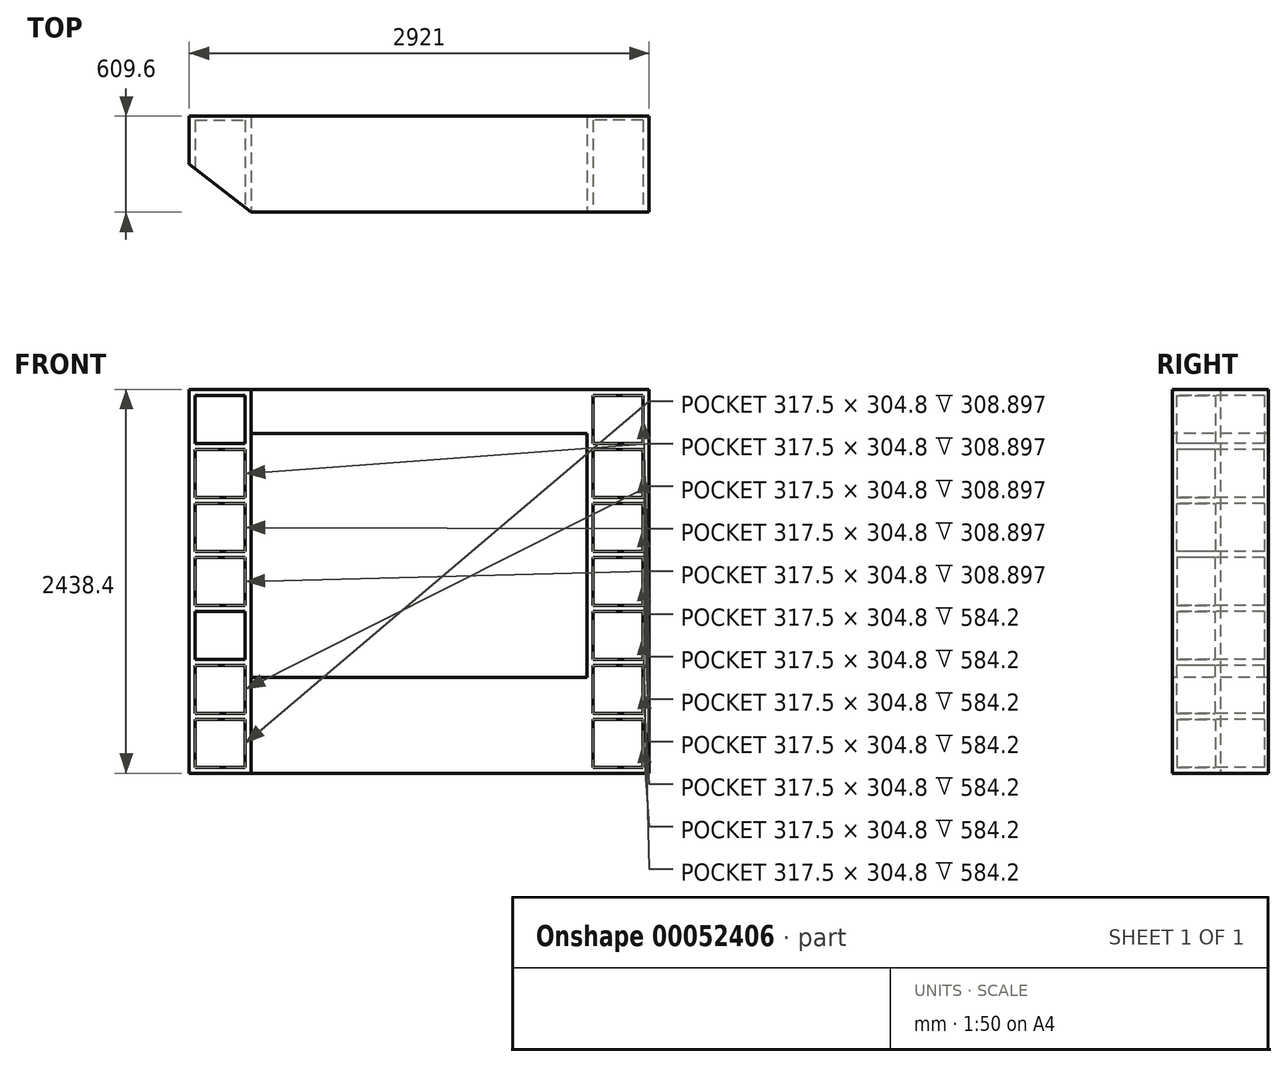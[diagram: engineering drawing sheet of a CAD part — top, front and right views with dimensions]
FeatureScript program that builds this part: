
annotation { "Feature Type Name" : "Feature", "Feature Type Description" : "" }
export const myFeature = defineFeature(function(context is Context, id is Id, definition is map)
    precondition{}
    {
        {
            var Q0;
            Q0=qCreatedBy(makeId("Top.planeOp"),FACE);
            var sketch = newSketch(context, id + "F0", { "sketchPlane" : qUnion([Q0])});
            skLineSegment(sketch, "E0", {"start": v(-1460.5, 0) * mm, "end": v(1460.5, 0) * mm});
            skLineSegment(sketch, "E1", {"start": v(-1460.5, 0) * mm, "end": v(-1460.5, -304.8) * mm});
            skLineSegment(sketch, "E2", {"start": v(1460.5, 0) * mm, "end": v(1460.5, -304.8) * mm});
            skLineSegment(sketch, "E3", {"start": v(-1066.8, -609.6) * mm, "end": v(-1460.5, -304.8) * mm});
            skLineSegment(sketch, "E4", {"start": v(0, -609.6) * mm, "end": v(1460.5, -609.6) * mm});
            skLineSegment(sketch, "E5", {"start": v(0, -609.6) * mm, "end": v(-1066.8, -609.6) * mm});
            skLineSegment(sketch, "E6", {"start": v(1460.5, -304.8) * mm, "end": v(1460.5, -609.6) * mm});
            skPoint(sketch, "E7.start.orphan", {"position": v(1066.8, -609.6) * mm});
            skSolve(sketch);
        }
        {
            var Q0;
            Q0=makeQuery(id+"F0.imprint","IMPRINT",FACE,{"disambiguationData":[TD([[makeQuery(id+"F0.imprint","IMPRINT",EDGE,{"derivedFrom":sQuery(id+"F0.wireOp",EDGE,"E0")}),-1.0]])]});
            extrude(context, id + "F1", {"entities" : qUnion([Q0]), "depth" : 2438.4 * mm});
        }
        {
            var Q0;
            Q0=makeQuery(id+"F1.opExtrude","SWEPT_FACE",FACE,{"disambiguationData":[OSD([sQuery(id+"F0.wireOp",EDGE,"E4"),sQuery(id+"F0.wireOp",EDGE,"E5")])]});
            var sketch = newSketch(context, id + "F2", { "sketchPlane" : qUnion([Q0])});
            skLineSegment(sketch, "E8", {"start": v(-1066.8, 609.6) * mm, "end": v(-1066.8, 2159) * mm});
            skLineSegment(sketch, "E9", {"start": v(-1066.8, 2159) * mm, "end": v(1066.8, 2159) * mm});
            skLineSegment(sketch, "E10", {"start": v(1066.8, 609.6) * mm, "end": v(-1066.8, 609.6) * mm});
            skLineSegment(sketch, "E11", {"start": v(1066.8, 2159) * mm, "end": v(1066.8, 609.6) * mm});
            skSolve(sketch);
        }
        {
            var Q0;
            Q0=makeQuery(id+"F2.imprint","IMPRINT",FACE,{"disambiguationData":[TD([[makeQuery(id+"F2.imprint","IMPRINT",EDGE,{"derivedFrom":sQuery(id+"F2.wireOp",EDGE,"E8")}),1.0]])]});
            extrude(context, id + "F3", {"entities" : qUnion([Q0]), "operationType" : NewBodyOperationType.REMOVE, "oppositeDirection" : true, "depth" : 609.6 * mm});
        }
        {
            var Q0;
            {var subQ2=sQuery(id+"F0.wireOp",EDGE,"E5");var subQ3=sQuery(id+"F0.wireOp",EDGE,"E4");Q0=makeQuery(id+"F3.boolean.opBoolean","SPLIT",FACE,{"disambiguationData":[TD([makeQuery(id+"F3.opExtrude","SWEPT_FACE",FACE,{"disambiguationData":[OSD([sQuery(id+"F2.wireOp",EDGE,"E10")])]})])],"derivedFrom":makeQuery(id+"F1.opExtrude","SWEPT_FACE",FACE,{"disambiguationData":[OSD([subQ3,subQ2])]})});}
            var sketch = newSketch(context, id + "F4", { "sketchPlane" : qUnion([Q0])});
            skLineSegment(sketch, "E12", {"start": v(1104.9, 38.1) * mm, "end": v(1422.4, 38.1) * mm});
            skLineSegment(sketch, "E13", {"start": v(1104.9, 342.9) * mm, "end": v(1422.4, 342.9) * mm});
            skLineSegment(sketch, "E14", {"start": v(1422.4, 342.9) * mm, "end": v(1104.9, 342.9) * mm});
            skLineSegment(sketch, "E15", {"start": v(1104.9, 1028.7) * mm, "end": v(1422.4, 1028.7) * mm});
            skLineSegment(sketch, "E16", {"start": v(1104.9, 342.9) * mm, "end": v(1104.9, 38.1) * mm});
            skLineSegment(sketch, "E17", {"start": v(1422.4, 342.9) * mm, "end": v(1422.4, 38.1) * mm});
            skLineSegment(sketch, "E18", {"start": v(1104.9, 381) * mm, "end": v(1422.4, 381) * mm});
            skLineSegment(sketch, "E19", {"start": v(1422.4, 381) * mm, "end": v(1422.4, 685.8) * mm});
            skLineSegment(sketch, "E20", {"start": v(1104.9, 381) * mm, "end": v(1104.9, 685.8) * mm});
            skLineSegment(sketch, "E21", {"start": v(1422.4, 685.8) * mm, "end": v(1104.9, 685.8) * mm});
            skLineSegment(sketch, "E22", {"start": v(1104.9, 723.9) * mm, "end": v(1422.4, 723.9) * mm});
            skLineSegment(sketch, "E23", {"start": v(1422.4, 723.9) * mm, "end": v(1422.4, 1028.7) * mm});
            skLineSegment(sketch, "E24", {"start": v(1104.9, 1028.7) * mm, "end": v(1104.9, 723.9) * mm});
            skLineSegment(sketch, "E25", {"start": v(1104.9, 1066.8) * mm, "end": v(1422.4, 1066.8) * mm});
            skLineSegment(sketch, "E26", {"start": v(1422.4, 1066.8) * mm, "end": v(1422.4, 1371.6) * mm});
            skLineSegment(sketch, "E27", {"start": v(1422.4, 1371.6) * mm, "end": v(1104.9, 1371.6) * mm});
            skLineSegment(sketch, "E28", {"start": v(1104.9, 1371.6) * mm, "end": v(1104.9, 1066.8) * mm});
            skLineSegment(sketch, "E29", {"start": v(1422.4, 1409.7) * mm, "end": v(1104.9, 1409.7) * mm});
            skLineSegment(sketch, "E30", {"start": v(1104.9, 1409.7) * mm, "end": v(1104.9, 1714.5) * mm});
            skLineSegment(sketch, "E31", {"start": v(1104.9, 1714.5) * mm, "end": v(1422.4, 1714.5) * mm});
            skLineSegment(sketch, "E32", {"start": v(1422.4, 1714.5) * mm, "end": v(1422.4, 1409.7) * mm});
            skLineSegment(sketch, "E33", {"start": v(1104.9, 1752.6) * mm, "end": v(1422.4, 1752.6) * mm});
            skLineSegment(sketch, "E34", {"start": v(1422.4, 1752.6) * mm, "end": v(1422.4, 2057.4) * mm});
            skLineSegment(sketch, "E35", {"start": v(1422.4, 2057.4) * mm, "end": v(1104.9, 2057.4) * mm});
            skLineSegment(sketch, "E36", {"start": v(1104.9, 2057.4) * mm, "end": v(1104.9, 1752.6) * mm});
            skLineSegment(sketch, "E37", {"start": v(1422.4, 2095.5) * mm, "end": v(1104.9, 2095.5) * mm});
            skLineSegment(sketch, "E38", {"start": v(1104.9, 2095.5) * mm, "end": v(1104.9, 2400.3) * mm});
            skLineSegment(sketch, "E39", {"start": v(1104.9, 2400.3) * mm, "end": v(1422.4, 2400.3) * mm});
            skLineSegment(sketch, "E40", {"start": v(1422.4, 2400.3) * mm, "end": v(1422.4, 2095.5) * mm});
            skLineSegment(sketch, "E41", {"start": v(1066.8, 609.6) * mm, "end": v(1066.8, 1171.43) * mm});
            skLineSegment(sketch, "E42", {"start": v(0, 0) * mm, "end": v(0, 823.78) * mm});
            skLineSegment(sketch, "E43.MirrorCS", {"start": v(-1422.4, 2095.5) * mm, "end": v(-1104.9, 2095.5) * mm});
            skLineSegment(sketch, "E44.MirrorCS", {"start": v(-1422.4, 685.8) * mm, "end": v(-1104.9, 685.8) * mm});
            skLineSegment(sketch, "E45.MirrorCS", {"start": v(-1422.4, 2057.4) * mm, "end": v(-1104.9, 2057.4) * mm});
            skLineSegment(sketch, "E46.MirrorCS", {"start": v(-1104.9, 342.9) * mm, "end": v(-1422.4, 342.9) * mm});
            skLineSegment(sketch, "E47.MirrorCS", {"start": v(-1104.9, 723.9) * mm, "end": v(-1422.4, 723.9) * mm});
            skLineSegment(sketch, "E48.MirrorCS", {"start": v(-1104.9, 2095.5) * mm, "end": v(-1104.9, 2400.3) * mm});
            skLineSegment(sketch, "E49.MirrorCS", {"start": v(-1422.4, 723.9) * mm, "end": v(-1422.4, 1028.7) * mm});
            skLineSegment(sketch, "E50.MirrorCS", {"start": v(-1422.4, 342.9) * mm, "end": v(-1422.4, 38.1) * mm});
            skLineSegment(sketch, "E51.MirrorCS", {"start": v(-1104.9, 1028.7) * mm, "end": v(-1104.9, 723.9) * mm});
            skLineSegment(sketch, "E52.MirrorCS", {"start": v(-1104.9, 1752.6) * mm, "end": v(-1422.4, 1752.6) * mm});
            skLineSegment(sketch, "E53.MirrorCS", {"start": v(-1422.4, 1409.7) * mm, "end": v(-1104.9, 1409.7) * mm});
            skLineSegment(sketch, "E54.MirrorCS", {"start": v(-1104.9, 1409.7) * mm, "end": v(-1104.9, 1714.5) * mm});
            skLineSegment(sketch, "E55.MirrorCS", {"start": v(-1422.4, 1752.6) * mm, "end": v(-1422.4, 2057.4) * mm});
            skLineSegment(sketch, "E56.MirrorCS", {"start": v(-1104.9, 381) * mm, "end": v(-1104.9, 685.8) * mm});
            skLineSegment(sketch, "E57.MirrorCS", {"start": v(-1422.4, 381) * mm, "end": v(-1422.4, 685.8) * mm});
            skLineSegment(sketch, "E58.MirrorCS", {"start": v(-1104.9, 381) * mm, "end": v(-1422.4, 381) * mm});
            skLineSegment(sketch, "E59.MirrorCS", {"start": v(-1422.4, 342.9) * mm, "end": v(-1104.9, 342.9) * mm});
            skLineSegment(sketch, "E60.MirrorCS", {"start": v(-1104.9, 1028.7) * mm, "end": v(-1422.4, 1028.7) * mm});
            skLineSegment(sketch, "E61.MirrorCS", {"start": v(-1422.4, 1714.5) * mm, "end": v(-1422.4, 1409.7) * mm});
            skLineSegment(sketch, "E62.MirrorCS", {"start": v(-1422.4, 2400.3) * mm, "end": v(-1422.4, 2095.5) * mm});
            skLineSegment(sketch, "E63.MirrorCS", {"start": v(-1104.9, 1371.6) * mm, "end": v(-1104.9, 1066.8) * mm});
            skLineSegment(sketch, "E64.MirrorCS", {"start": v(-1104.9, 1066.8) * mm, "end": v(-1422.4, 1066.8) * mm});
            skLineSegment(sketch, "E65.MirrorCS", {"start": v(-1422.4, 1371.6) * mm, "end": v(-1104.9, 1371.6) * mm});
            skLineSegment(sketch, "E66.MirrorCS", {"start": v(-1104.9, 2400.3) * mm, "end": v(-1422.4, 2400.3) * mm});
            skLineSegment(sketch, "E67.MirrorCS", {"start": v(-1422.4, 1066.8) * mm, "end": v(-1422.4, 1371.6) * mm});
            skLineSegment(sketch, "E68.MirrorCS", {"start": v(-1104.9, 2057.4) * mm, "end": v(-1104.9, 1752.6) * mm});
            skLineSegment(sketch, "E69.MirrorCS", {"start": v(-1104.9, 1714.5) * mm, "end": v(-1422.4, 1714.5) * mm});
            skLineSegment(sketch, "E70.MirrorCS", {"start": v(-1104.9, 342.9) * mm, "end": v(-1104.9, 38.1) * mm});
            skLineSegment(sketch, "E71.MirrorCS", {"start": v(-1104.9, 38.1) * mm, "end": v(-1422.4, 38.1) * mm});
            skSolve(sketch);
        }
        {
            var Q0;
            Q0 = qSketchRegion(id + "F4", true);
            extrude(context, id + "F5", {"entities" : qUnion([Q0]), "operationType" : NewBodyOperationType.REMOVE, "oppositeDirection" : true, "depth" : 584.2 * mm});
        }
    });
